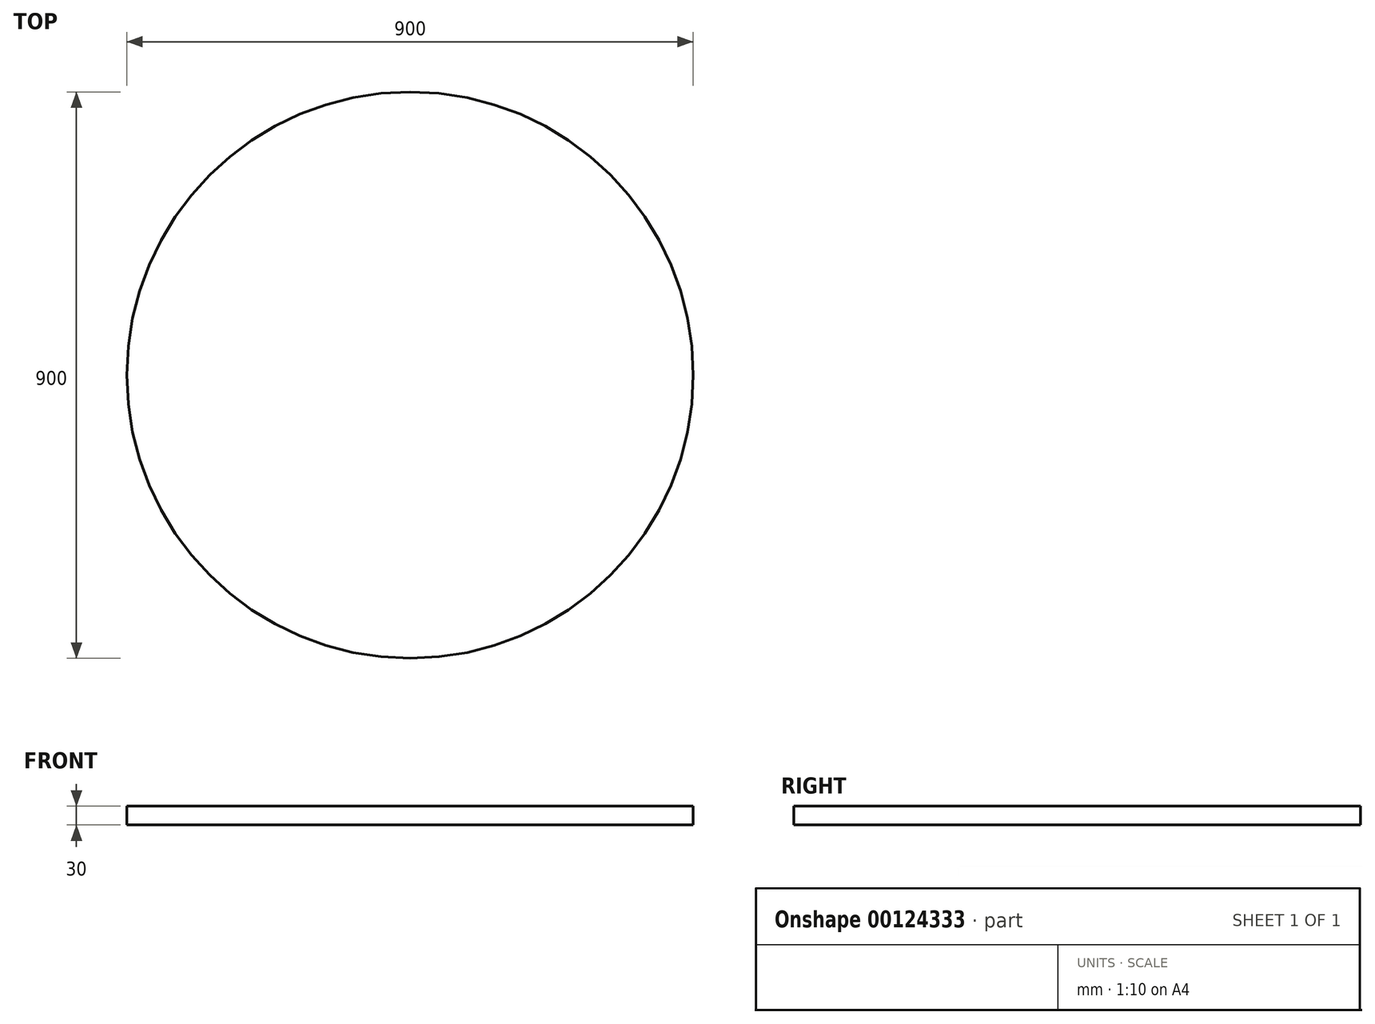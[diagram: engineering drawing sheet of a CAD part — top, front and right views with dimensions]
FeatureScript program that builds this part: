
annotation { "Feature Type Name" : "Feature", "Feature Type Description" : "" }
export const myFeature = defineFeature(function(context is Context, id is Id, definition is map)
    precondition{}
    {
        {
            var Q0;
            Q0=qCreatedBy(makeId("Top.planeOp"),FACE);
            var sketch = newSketch(context, id + "F0", { "sketchPlane" : qUnion([Q0])});
            skCircle(sketch, "E0", {"center": v(0, 0) * mm, "radius": 450 * mm});
            skSolve(sketch);
        }
        {
            var Q0;
            Q0=makeQuery(id+"F0.imprint","IMPRINT",FACE,{"disambiguationData":[TD([[makeQuery(id+"F0.imprint","IMPRINT",EDGE,{"derivedFrom":sQuery(id+"F0.wireOp",EDGE,"E0")}),1.0]])]});
            extrude(context, id + "F1", {"entities" : qUnion([Q0]), "depth" : 30 * mm});
        }
    });
